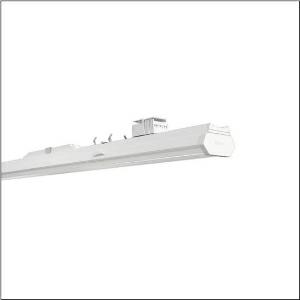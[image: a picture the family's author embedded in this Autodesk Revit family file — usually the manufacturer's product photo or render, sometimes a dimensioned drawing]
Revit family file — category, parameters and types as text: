
# Revit family: licross_r__11_protected_mo_51td12dn495g3s4_8e8e
name_source: partatom
category: Lighting Fixtures
units: mm (PartAtom-declared; Revit-internal decimal feet)

## family parameters
Cut with Voids When Loaded = No
Host = Face
Light Source = No
Part Type = Normal
Room Calculation Point = No
Round Connector Dimension = Use Diameter
Shared = No

## types (1)
- --- (1 x LED, 980 lm, 6.8 W, 4000K)
    Apparent Load = 7 VA
    CIE Flux Codes = 73 92 98 99 100
    Color Rendering = 80
    Color Temperature = 4000K
    Default Elevation = 1800 mm
    Description = Licross® 11 Protected MO, luminaire insert, of sheet steel, galvanised, coil coated, white, length: 1.500mm, width: 90mm, height: 101mm, LED rated luminous flux: 9.980lm, light colour: 840, control gear: DALI 2, with plug, 6-pole, with phase selection, for trunking rail, 9 or 11-core, mains connection: 220..240V, AC, 50/60Hz, rated input power: 61W, for trunking rail, 9-/11-core, halogen-free wiring, for emergency light function, converter,control gear: single battery element, battery: LiFePO4, 9Ah, primary light control with lens, of plastic, primary optical cover: cover, of PMMA, light emission: direct distribution, primary light characteristic: symmetric, protection rating (complete): IP54, insulation class (complete): insulation class I (protective earthing), certification: CE, UKCA, protection symbol: D if used in an environment with non-conductive dust loads with corresponding accessories, impact resistance: IK06, permissible ambient temperature for indoor applications: +5..+35°C, standard: EN 60598-2-22, LABS conformity tested according to VDMA 24364:2018-05, reducing of maximum allowable ambient temperature of 5°C with ceiling mounting, corresponds to IFS (International Featured Standards) requirements for safety and quality in the food industry, packaging unit: 1 piece
    Height = 92 mm
    Lamp = 1 x LED
    Lamp Light Flux = 980 lm
    Lamp Power = 6.8 W
    Lamp count = 1
    Length = 1500 mm
    Luminous efficacy = 144 lm/W
    Manufacturer = Siteco
    ModVariant = No
    Model = 51TD12DN495G3S4
    Mounting Place = Ceiling
    Mounting Type = Pendant
    Number of Poles = 1
    OnlyDefault = Yes
    Power Factor = 1
    Product Name = Licross® 11 Protected MO
    Product group = luminaire insert
    ProductGroupID = 902
    Protection Class = Protection class I
    Protection Degree = IP 54
    RLX_Detail_Level = 1
    RLX_Emergency_Light_Flux = 0 lm
    RLX_Emergency_Type = 0
    RLX_Emergency_Type_DB = No
    RlxData = <blob elided: 24825 chars, md5=e91cae33>
    Socket = socket
    Standby Power = 0 W
    System Light Flux = 980 lm
    System Power = 7 W
    Type Comments = : emergency light operation: 3 h
    Type Image = l_1256145.jpg
    URL = http://relux.com
    VarID = @adj_090510
    Voltage = 0 V
    Weight = 0.00 kg
    Width = 88 mm

## geometry (parser evidence)
native form markers: Blend x4, Sweep x11
no freeform markers — native parametric forms only
